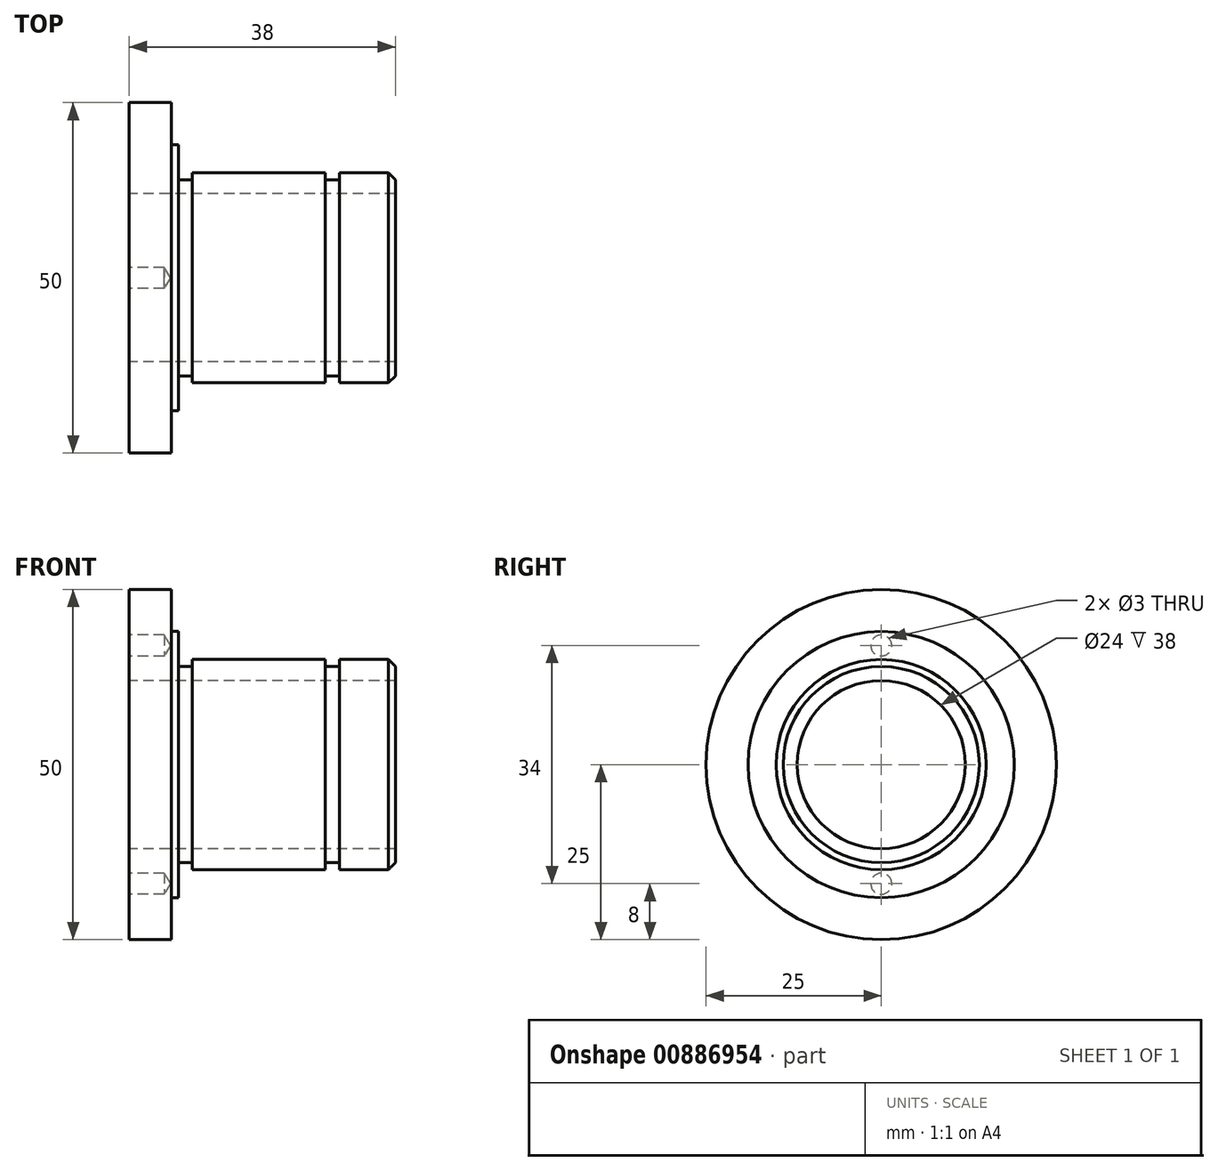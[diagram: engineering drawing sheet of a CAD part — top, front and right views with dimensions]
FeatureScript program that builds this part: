
annotation { "Feature Type Name" : "Feature", "Feature Type Description" : "" }
export const myFeature = defineFeature(function(context is Context, id is Id, definition is map)
    precondition{}
    {
        {
            var Q0;
            Q0=qCreatedBy(makeId("Front.planeOp"),FACE);
            var sketch = newSketch(context, id + "F0", { "sketchPlane" : qUnion([Q0])});
            skLineSegment(sketch, "E0", {"start": v(-7.44, 0) * mm, "end": v(40.35, 0) * mm, "construction": true});
            skLineSegment(sketch, "E1", {"start": v(0, 12) * mm, "end": v(0, 25) * mm});
            skLineSegment(sketch, "E2", {"start": v(0, 25) * mm, "end": v(6, 25) * mm});
            skLineSegment(sketch, "E3", {"start": v(6, 25) * mm, "end": v(6, 19) * mm});
            skLineSegment(sketch, "E4", {"start": v(6, 19) * mm, "end": v(7, 19) * mm});
            skLineSegment(sketch, "E5", {"start": v(7, 19) * mm, "end": v(7, 14) * mm});
            skLineSegment(sketch, "E6", {"start": v(7, 14) * mm, "end": v(9, 14) * mm});
            skLineSegment(sketch, "E7", {"start": v(9, 14) * mm, "end": v(9, 15) * mm});
            skLineSegment(sketch, "E8", {"start": v(9, 15) * mm, "end": v(28, 15) * mm});
            skLineSegment(sketch, "E9", {"start": v(28, 15) * mm, "end": v(28, 14) * mm});
            skLineSegment(sketch, "E10", {"start": v(28, 14) * mm, "end": v(30, 14) * mm});
            skLineSegment(sketch, "E11", {"start": v(30, 14) * mm, "end": v(30, 15) * mm});
            skLineSegment(sketch, "E12", {"start": v(30, 15) * mm, "end": v(38, 15) * mm});
            skLineSegment(sketch, "E13", {"start": v(38, 15) * mm, "end": v(38, 12) * mm});
            skLineSegment(sketch, "E14", {"start": v(38, 12) * mm, "end": v(0, 12) * mm});
            skSolve(sketch);
        }
        {
            var Q0;
            Q0 = qSketchRegion(id + "F0", true);
            var Q1;
            Q1=sQuery(id+"F0.wireOp",EDGE,"E0");
            revolve(context, id + "F1", {"surfaceOperationType" : NewSurfaceOperationType.NEW, "entities" : qUnion([Q0]), "axis" : qUnion([Q1]), "revolveType" : RevolveType.FULL});
        }
        {
            var Q0;
            Q0=makeQuery(id+"F1.opRevolve","SWEPT_EDGE",EDGE,{"disambiguationData":[OSD([sQuery(id+"F0.wireOp",EDGE,"E12"),sQuery(id+"F0.wireOp",EDGE,"E13")])]});
            chamfer(context, id + "F2", {"entities" : qUnion([Q0]), "width" : 1 * mm, "tangentPropagation" : true});
        }
        {
            var Q0;
            Q0=makeQuery(id+"F1.opRevolve","SWEPT_FACE",FACE,{"disambiguationData":[OSD([sQuery(id+"F0.wireOp",EDGE,"E1")])]});
            var sketch = newSketch(context, id + "F3", { "sketchPlane" : qUnion([Q0])});
            skLineSegment(sketch, "E15", {"start": v(0, 0) * mm, "end": v(6.65, 0) * mm, "construction": true});
            skLineSegment(sketch, "E16", {"start": v(0, -17) * mm, "end": v(0, 17) * mm, "construction": true});
            skPoint(sketch, "E17", {"position": v(0, 17) * mm});
            skPoint(sketch, "E18", {"position": v(0, -17) * mm});
            skSolve(sketch);
        }
        {
            var Q0;
            Q0=sQuery(id+"F3.wireOp",VERTEX,"E17");
            var Q1;
            Q1=sQuery(id+"F3.wireOp",VERTEX,"E18");
            var Q2;
            Q2=makeQuery(id+"F1.opRevolve","SWEPT_BODY",BODY,{"disambiguationData":[OSD([sQuery(id+"F0.wireOp",EDGE,"E1"),sQuery(id+"F0.wireOp",EDGE,"E2"),sQuery(id+"F0.wireOp",EDGE,"E3"),sQuery(id+"F0.wireOp",EDGE,"E4"),sQuery(id+"F0.wireOp",EDGE,"E5"),sQuery(id+"F0.wireOp",EDGE,"E6"),sQuery(id+"F0.wireOp",EDGE,"E7"),sQuery(id+"F0.wireOp",EDGE,"E8"),sQuery(id+"F0.wireOp",EDGE,"E9"),sQuery(id+"F0.wireOp",EDGE,"E10"),sQuery(id+"F0.wireOp",EDGE,"E11"),sQuery(id+"F0.wireOp",EDGE,"E12"),sQuery(id+"F0.wireOp",EDGE,"E13"),sQuery(id+"F0.wireOp",EDGE,"E14")])]});
            hole(context, id + "F4", {"style" : HoleStyle.SIMPLE, "endStyle" : HoleEndStyle.BLIND, "holeDiameter" : 3 * mm, "majorDiameter" : 5 * mm, "holeDepth" : 5 * mm, "tappedDepth" : 12 * mm, "tapClearance" : 3, "startFromSketch" : true, "locations" : qUnion([Q0, Q1]), "scope" : qUnion([Q2])});
        }
    });
